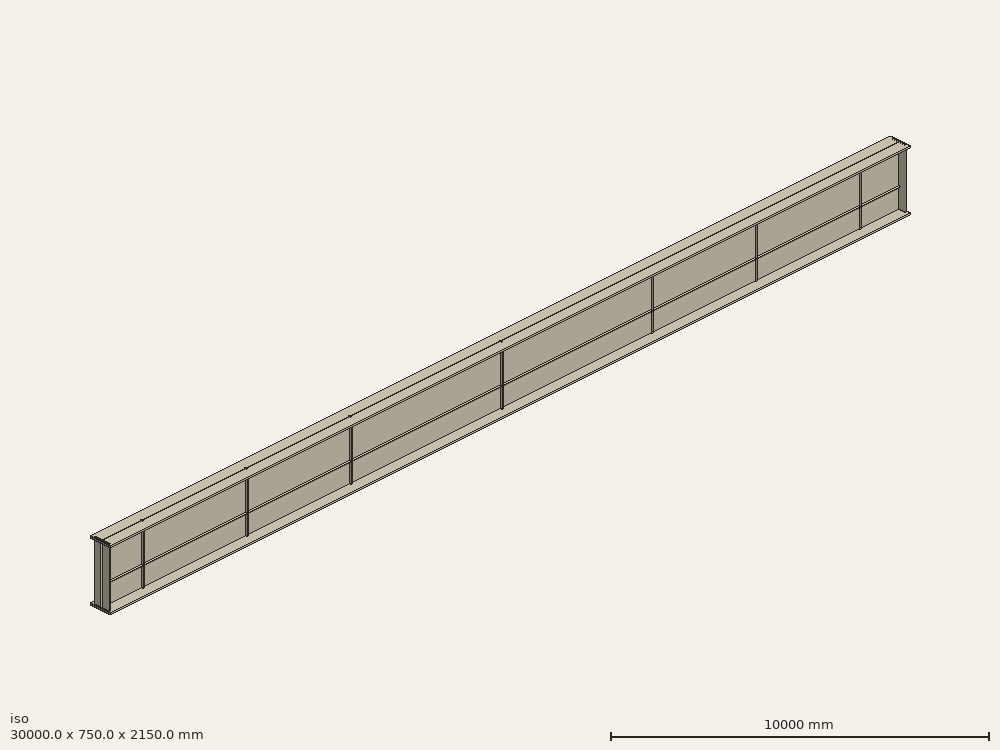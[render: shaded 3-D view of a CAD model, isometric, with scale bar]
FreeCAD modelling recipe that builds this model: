
FCSTD DOCUMENT  (FreeCAD 0.21R33771 (Git))
Label: Plate_girder_EC3_ts
License: All rights reserved
LicenseURL: http://en.wikipedia.org/wiki/All_rights_reserved
objects: Sketcher::SketchObject×13, Part::Extrusion×13, Fem::ConstraintForce×5, Fem::ConstraintDisplacement×2, Fem::FemSolverObjectPython×1, App::MaterialObjectPython×1, Part::Feature×1, Part::FeaturePython×1, Fem::FemMeshObjectPython×1, Fem::FemAnalysis×1
note: 28 computed .brp shape members not serialized (recipe doc carries the construction recipe); baked Part::Feature solids carry a one-line shape summary decoded from their .brp

FEATURE [Fem::FemSolverObjectPython] SolverCcxTools  # FEM object (typed FeaturePython)
  AnalysisType = 4
  BeamShellResultOutput3D = false
  BucklingFactors = 4
  EigenmodeHighLimit = 1000000
  EigenmodeLowLimit = 0
  EigenmodesCount = 10
  GeometricalNonlinearity = 0
  IterationsControlParameterCutb = 0.25,0.5,0.75,0.85,,,1.5,
  IterationsControlParameterIter = 4,8,9,200,10,400,,200,,
  IterationsControlParameterTimeUse = false
  IterationsThermoMechMaximum = 2000
  IterationsUserDefinedIncrementations = false
  IterationsUserDefinedTimeStepLength = false
  MaterialNonlinearity = 0
  MatrixSolverType = 0
  SplitInputWriter = true
  ThermoMechSteadyState = true
  TimeEnd = 1
  TimeInitialStep = 0.01
FEATURE [App::MaterialObjectPython] MaterialSolid  # material (typed FeaturePython)
  Category = 0
  Material = AuthorAndLicense=(c) 2014 M. Münch - GNU Lesser General Public License (LGPL),CardName=Steel-St-E-315,Density=7800 kg/m^3,Father=Metal,+13 more (map truncated)
FEATURE [Sketcher::SketchObject] Sketch001  label="end stiffener"
  FullyConstrained = true
  Placement = pos=(0,0,0) rot=(0.57735,0.57735,0.57735;2.0944rad)
  sketch-geometry (4):
    g0: LineSegment StartX=87.5 StartY=2100 StartZ=0 EndX=662.5 EndY=2100 EndZ=0
    g1: LineSegment StartX=662.5 StartY=2100 StartZ=0 EndX=662.5 EndY=0 EndZ=0
    g2: LineSegment StartX=662.5 StartY=0 StartZ=0 EndX=87.5 EndY=0 EndZ=0
    g3: LineSegment StartX=87.5 StartY=0 StartZ=0 EndX=87.5 EndY=2100 EndZ=0
  constraints (12):
    c: Coincident(g0,g1)
    c: Coincident(g1,g2)
    c: Coincident(g2,g3)
    c: Coincident(g3,g0)
    c: Horizontal(g0)
    c: Horizontal(g2)
    c: Vertical(g1)
    c: Vertical(g3)
    c: DistanceY(g1,g1) = 2100
    c: PointOnObject(g2,g-1)
    c: DistanceX(g2,g2) = 575
    c: DistanceX(g-1,g2) = 87.5
FEATURE [Sketcher::SketchObject] Sketch002  label="stiffener"
  FullyConstrained = true
  Placement = pos=(0,0,0) rot=(0.57735,0.57735,0.57735;2.0944rad)
  sketch-geometry (4):
    g0: LineSegment StartX=287.5 StartY=2100 StartZ=0 EndX=462.5 EndY=2100 EndZ=0
    g1: LineSegment StartX=462.5 StartY=2100 StartZ=0 EndX=462.5 EndY=0 EndZ=0
    g2: LineSegment StartX=462.5 StartY=0 StartZ=0 EndX=287.5 EndY=0 EndZ=0
    g3: LineSegment StartX=287.5 StartY=0 StartZ=0 EndX=287.5 EndY=2100 EndZ=0
  constraints (12):
    c: Coincident(g0,g1)
    c: Coincident(g1,g2)
    c: Coincident(g2,g3)
    c: Coincident(g3,g0)
    c: Horizontal(g0)
    c: Horizontal(g2)
    c: Vertical(g1)
    c: Vertical(g3)
    c: DistanceY(g1,g1) = 2100
    c: PointOnObject(g2,g-1)
    c: DistanceX(g0,g0) = 175
    c: DistanceX(g-1,g2) = 287.5
FEATURE [Sketcher::SketchObject] Sketch003
  FullyConstrained = true
  sketch-geometry (4):
    g0: LineSegment StartX=0 StartY=462.5 StartZ=0 EndX=175 EndY=462.5 EndZ=0
    g1: LineSegment StartX=175 StartY=462.5 StartZ=0 EndX=175 EndY=287.5 EndZ=0
    g2: LineSegment StartX=175 StartY=287.5 StartZ=0 EndX=0 EndY=287.5 EndZ=0
    g3: LineSegment StartX=0 StartY=287.5 StartZ=0 EndX=0 EndY=462.5 EndZ=0
  constraints (12):
    c: Coincident(g0,g1)
    c: Coincident(g1,g2)
    c: Coincident(g2,g3)
    c: Coincident(g3,g0)
    c: Horizontal(g0)
    c: Horizontal(g2)
    c: Vertical(g1)
    c: Vertical(g3)
    c: DistanceX(g0,g0) = 175
    c: DistanceY(g1,g1) = 175
    c: PointOnObject(g2,g-2)
    c: DistanceY(g-1,g2) = 287.5
FEATURE [Part::Extrusion] Extrude001  label="load pad"
  Base = -> Sketch003
  Dir = (0,0,1)
  DirMode = 2
  FaceMakerClass = Part::FaceMakerBullseye
  LengthFwd = 0
  LengthRev = 50
  Placement = pos=(9262.5,0,0) rot=(0,0,1;0rad)
  Solid = true
  Symmetric = false
FEATURE [Part::Extrusion] Extrude002  label="stiffener001"
  Base = -> Sketch002
  Dir = (1,0,0)
  DirMode = 2
  FaceMakerClass = Part::FaceMakerBullseye
  LengthFwd = 15
  LengthRev = 0
  Placement = pos=(1542.5,0,0) rot=(0,0,1;0rad)
  Solid = true
  Symmetric = false
FEATURE [Part::Extrusion] Extrude003  label="end stiffener001"
  Base = -> Sketch001
  Dir = (1,0,0)
  DirMode = 2
  FaceMakerClass = Part::FaceMakerBullseye
  LengthFwd = 24
  LengthRev = 0
  Placement = pos=(50,0,0) rot=(0,0,1;0rad)
  Solid = true
  Symmetric = false
FEATURE [Sketcher::SketchObject] Sketch004  label="end stiffener003"
  FullyConstrained = true
  Placement = pos=(0,0,0) rot=(0.57735,0.57735,0.57735;2.0944rad)
  sketch-geometry (4):
    g0: LineSegment StartX=87.5 StartY=2100 StartZ=0 EndX=662.5 EndY=2100 EndZ=0
    g1: LineSegment StartX=662.5 StartY=2100 StartZ=0 EndX=662.5 EndY=0 EndZ=0
    g2: LineSegment StartX=662.5 StartY=0 StartZ=0 EndX=87.5 EndY=0 EndZ=0
    g3: LineSegment StartX=87.5 StartY=0 StartZ=0 EndX=87.5 EndY=2100 EndZ=0
  constraints (12):
    c: Coincident(g0,g1)
    c: Coincident(g1,g2)
    c: Coincident(g2,g3)
    c: Coincident(g3,g0)
    c: Horizontal(g0)
    c: Horizontal(g2)
    c: Vertical(g1)
    c: Vertical(g3)
    c: DistanceY(g1,g1) = 2100
    c: PointOnObject(g2,g-1)
    c: DistanceX(g2,g2) = 575
    c: DistanceX(g-1,g2) = 87.5
FEATURE [Part::Extrusion] Extrude004  label="end stiffener002"
  Base = -> Sketch004
  Dir = (1,0,0)
  DirMode = 2
  FaceMakerClass = Part::FaceMakerBullseye
  LengthFwd = 24
  LengthRev = 0
  Placement = pos=(29930,0,0) rot=(0,0,1;0rad)
  Solid = true
  Symmetric = false
FEATURE [Sketcher::SketchObject] Sketch005  label="stiffener003"
  FullyConstrained = true
  Placement = pos=(0,0,0) rot=(0.57735,0.57735,0.57735;2.0944rad)
  sketch-geometry (4):
    g0: LineSegment StartX=287.5 StartY=2100 StartZ=0 EndX=462.5 EndY=2100 EndZ=0
    g1: LineSegment StartX=462.5 StartY=2100 StartZ=0 EndX=462.5 EndY=0 EndZ=0
    g2: LineSegment StartX=462.5 StartY=0 StartZ=0 EndX=287.5 EndY=0 EndZ=0
    g3: LineSegment StartX=287.5 StartY=0 StartZ=0 EndX=287.5 EndY=2100 EndZ=0
  constraints (12):
    c: Coincident(g0,g1)
    c: Coincident(g1,g2)
    c: Coincident(g2,g3)
    c: Coincident(g3,g0)
    c: Horizontal(g0)
    c: Horizontal(g2)
    c: Vertical(g1)
    c: Vertical(g3)
    c: DistanceY(g1,g1) = 2100
    c: PointOnObject(g2,g-1)
    c: DistanceX(g0,g0) = 175
    c: DistanceX(g-1,g2) = 287.5
FEATURE [Part::Extrusion] Extrude005  label="stiffener002"
  Base = -> Sketch005
  Dir = (1,0,0)
  DirMode = 2
  FaceMakerClass = Part::FaceMakerBullseye
  LengthFwd = 15
  LengthRev = 0
  Placement = pos=(5442.5,0,0) rot=(0,0,1;0rad)
  Solid = true
  Symmetric = false
FEATURE [Sketcher::SketchObject] Sketch006  label="stiffener005"
  FullyConstrained = true
  Placement = pos=(0,0,0) rot=(0.57735,0.57735,0.57735;2.0944rad)
  sketch-geometry (4):
    g0: LineSegment StartX=287.5 StartY=2100 StartZ=0 EndX=462.5 EndY=2100 EndZ=0
    g1: LineSegment StartX=462.5 StartY=2100 StartZ=0 EndX=462.5 EndY=0 EndZ=0
    g2: LineSegment StartX=462.5 StartY=0 StartZ=0 EndX=287.5 EndY=0 EndZ=0
    g3: LineSegment StartX=287.5 StartY=0 StartZ=0 EndX=287.5 EndY=2100 EndZ=0
  constraints (12):
    c: Coincident(g0,g1)
    c: Coincident(g1,g2)
    c: Coincident(g2,g3)
    c: Coincident(g3,g0)
    c: Horizontal(g0)
    c: Horizontal(g2)
    c: Vertical(g1)
    c: Vertical(g3)
    c: DistanceY(g1,g1) = 2100
    c: PointOnObject(g2,g-1)
    c: DistanceX(g0,g0) = 175
    c: DistanceX(g-1,g2) = 287.5
FEATURE [Part::Extrusion] Extrude006  label="stiffener004"
  Base = -> Sketch006
  Dir = (1,0,0)
  DirMode = 2
  FaceMakerClass = Part::FaceMakerBullseye
  LengthFwd = 15
  LengthRev = 0
  Placement = pos=(9342.5,0,0) rot=(0,0,1;0rad)
  Solid = true
  Symmetric = false
FEATURE [Sketcher::SketchObject] Sketch007  label="stiffener007"
  FullyConstrained = true
  Placement = pos=(0,0,0) rot=(0.57735,0.57735,0.57735;2.0944rad)
  sketch-geometry (4):
    g0: LineSegment StartX=287.5 StartY=2100 StartZ=0 EndX=462.5 EndY=2100 EndZ=0
    g1: LineSegment StartX=462.5 StartY=2100 StartZ=0 EndX=462.5 EndY=0 EndZ=0
    g2: LineSegment StartX=462.5 StartY=0 StartZ=0 EndX=287.5 EndY=0 EndZ=0
    g3: LineSegment StartX=287.5 StartY=0 StartZ=0 EndX=287.5 EndY=2100 EndZ=0
  constraints (12):
    c: Coincident(g0,g1)
    c: Coincident(g1,g2)
    c: Coincident(g2,g3)
    c: Coincident(g3,g0)
    c: Horizontal(g0)
    c: Horizontal(g2)
    c: Vertical(g1)
    c: Vertical(g3)
    c: DistanceY(g1,g1) = 2100
    c: PointOnObject(g2,g-1)
    c: DistanceX(g0,g0) = 175
    c: DistanceX(g-1,g2) = 287.5
FEATURE [Part::Extrusion] Extrude007  label="stiffener006"
  Base = -> Sketch007
  Dir = (1,0,0)
  DirMode = 2
  FaceMakerClass = Part::FaceMakerBullseye
  LengthFwd = 15
  LengthRev = 0
  Placement = pos=(14992.5,0,0) rot=(0,0,1;0rad)
  Solid = true
  Symmetric = false
FEATURE [Sketcher::SketchObject] Sketch008  label="stiffener009"
  FullyConstrained = true
  Placement = pos=(0,0,0) rot=(0.57735,0.57735,0.57735;2.0944rad)
  sketch-geometry (4):
    g0: LineSegment StartX=287.5 StartY=2100 StartZ=0 EndX=462.5 EndY=2100 EndZ=0
    g1: LineSegment StartX=462.5 StartY=2100 StartZ=0 EndX=462.5 EndY=0 EndZ=0
    g2: LineSegment StartX=462.5 StartY=0 StartZ=0 EndX=287.5 EndY=0 EndZ=0
    g3: LineSegment StartX=287.5 StartY=0 StartZ=0 EndX=287.5 EndY=2100 EndZ=0
  constraints (12):
    c: Coincident(g0,g1)
    c: Coincident(g1,g2)
    c: Coincident(g2,g3)
    c: Coincident(g3,g0)
    c: Horizontal(g0)
    c: Horizontal(g2)
    c: Vertical(g1)
    c: Vertical(g3)
    c: DistanceY(g1,g1) = 2100
    c: PointOnObject(g2,g-1)
    c: DistanceX(g0,g0) = 175
    c: DistanceX(g-1,g2) = 287.5
FEATURE [Part::Extrusion] Extrude008  label="stiffener008"
  Base = -> Sketch008
  Dir = (1,0,0)
  DirMode = 2
  FaceMakerClass = Part::FaceMakerBullseye
  LengthFwd = 15
  LengthRev = 0
  Placement = pos=(20642.5,0,0) rot=(0,0,1;0rad)
  Solid = true
  Symmetric = false
FEATURE [Sketcher::SketchObject] Sketch009  label="stiffener011"
  FullyConstrained = true
  Placement = pos=(0,0,0) rot=(0.57735,0.57735,0.57735;2.0944rad)
  sketch-geometry (4):
    g0: LineSegment StartX=287.5 StartY=2100 StartZ=0 EndX=462.5 EndY=2100 EndZ=0
    g1: LineSegment StartX=462.5 StartY=2100 StartZ=0 EndX=462.5 EndY=0 EndZ=0
    g2: LineSegment StartX=462.5 StartY=0 StartZ=0 EndX=287.5 EndY=0 EndZ=0
    g3: LineSegment StartX=287.5 StartY=0 StartZ=0 EndX=287.5 EndY=2100 EndZ=0
  constraints (12):
    c: Coincident(g0,g1)
    c: Coincident(g1,g2)
    c: Coincident(g2,g3)
    c: Coincident(g3,g0)
    c: Horizontal(g0)
    c: Horizontal(g2)
    c: Vertical(g1)
    c: Vertical(g3)
    c: DistanceY(g1,g1) = 2100
    c: PointOnObject(g2,g-1)
    c: DistanceX(g0,g0) = 175
    c: DistanceX(g-1,g2) = 287.5
FEATURE [Part::Extrusion] Extrude009  label="stiffener010"
  Base = -> Sketch009
  Dir = (1,0,0)
  DirMode = 2
  FaceMakerClass = Part::FaceMakerBullseye
  LengthFwd = 15
  LengthRev = 0
  Placement = pos=(24542.5,0,0) rot=(0,0,1;0rad)
  Solid = true
  Symmetric = false
FEATURE [Sketcher::SketchObject] Sketch010  label="stiffener013"
  FullyConstrained = true
  Placement = pos=(0,0,0) rot=(0.57735,0.57735,0.57735;2.0944rad)
  sketch-geometry (4):
    g0: LineSegment StartX=287.5 StartY=2100 StartZ=0 EndX=462.5 EndY=2100 EndZ=0
    g1: LineSegment StartX=462.5 StartY=2100 StartZ=0 EndX=462.5 EndY=0 EndZ=0
    g2: LineSegment StartX=462.5 StartY=0 StartZ=0 EndX=287.5 EndY=0 EndZ=0
    g3: LineSegment StartX=287.5 StartY=0 StartZ=0 EndX=287.5 EndY=2100 EndZ=0
  constraints (12):
    c: Coincident(g0,g1)
    c: Coincident(g1,g2)
    c: Coincident(g2,g3)
    c: Coincident(g3,g0)
    c: Horizontal(g0)
    c: Horizontal(g2)
    c: Vertical(g1)
    c: Vertical(g3)
    c: DistanceY(g1,g1) = 2100
    c: PointOnObject(g2,g-1)
    c: DistanceX(g0,g0) = 175
    c: DistanceX(g-1,g2) = 287.5
FEATURE [Part::Extrusion] Extrude010  label="stiffener012"
  Base = -> Sketch010
  Dir = (1,0,0)
  DirMode = 2
  FaceMakerClass = Part::FaceMakerBullseye
  LengthFwd = 15
  LengthRev = 0
  Placement = pos=(28442.5,0,0) rot=(0,0,1;0rad)
  Solid = true
  Symmetric = false
FEATURE [Sketcher::SketchObject] Sketch  label="girder"
  FullyConstrained = true
  Placement = pos=(0,0,0) rot=(0.57735,0.57735,0.57735;2.0944rad)
  sketch-geometry (16):
    g0: LineSegment StartX=750 StartY=2100 StartZ=0 EndX=750 EndY=2050 EndZ=0
    g1: LineSegment StartX=750 StartY=2050 StartZ=0 EndX=382.5 EndY=2050 EndZ=0
    g2: LineSegment StartX=382.5 StartY=2050 StartZ=0 EndX=382.5 EndY=50 EndZ=0
    g3: LineSegment StartX=382.5 StartY=50 StartZ=0 EndX=750 EndY=50 EndZ=0
    g4: LineSegment StartX=750 StartY=50 StartZ=0 EndX=750 EndY=0 EndZ=0
    g5: LineSegment StartX=0 StartY=0 StartZ=0 EndX=0 EndY=50 EndZ=0
    g6: LineSegment StartX=0 StartY=50 StartZ=0 EndX=367.5 EndY=50 EndZ=0
    g7: LineSegment StartX=367.5 StartY=50 StartZ=0 EndX=367.5 EndY=2050 EndZ=0
    g8: LineSegment StartX=367.5 StartY=2050 StartZ=0 EndX=0 EndY=2050 EndZ=0
    g9: LineSegment StartX=750 StartY=2100 StartZ=0 EndX=382.5 EndY=2100 EndZ=0
    g10: LineSegment StartX=750 StartY=0 StartZ=0 EndX=382.5 EndY=0 EndZ=0
    g11: LineSegment StartX=367.5 StartY=0 StartZ=0 EndX=0 EndY=0 EndZ=0
    g12: LineSegment StartX=382.5 StartY=2100 StartZ=0 EndX=367.5 EndY=2100 EndZ=0
    g13: LineSegment StartX=0 StartY=2050 StartZ=0 EndX=0 EndY=2100 EndZ=0
    g14: LineSegment StartX=367.5 StartY=0 StartZ=0 EndX=382.5 EndY=0 EndZ=0
    g15: LineSegment StartX=0 StartY=2100 StartZ=0 EndX=367.5 EndY=2100 EndZ=0
  constraints (48):
    c: Vertical(g0)
    c: Coincident(g0,g1)
    c: Horizontal(g1)
    c: Coincident(g1,g2)
    c: Vertical(g2)
    c: Coincident(g2,g3)
    c: Horizontal(g3)
    c: Coincident(g3,g4)
    c: PointOnObject(g4,g-1)
    c: Vertical(g5)
    c: Coincident(g5,g6)
    c: Horizontal(g6)
    c: Coincident(g6,g7)
    c: Vertical(g7)
    c: Coincident(g7,g8)
    c: Horizontal(g8)
    c: Vertical(g4)
    c: DistanceY(g0,g0) = 50
    c: DistanceX(g6,g6) = 367.5
    c: DistanceX(g3,g3) = 367.5
    c: DistanceY(g4,g4) = 50
    c: DistanceY(g5,g5) = 50
    c: DistanceY(g4,g0) = 2100
    c: DistanceX(g-1,g5) = 0
    c: Coincident(g9,g0)
    c: Horizontal(g9)
    c: Coincident(g10,g4)
    c: Horizontal(g10)
    c: Coincident(g11,g5)
    c: Horizontal(g11)
    c: Coincident(g12,g9)
    c: Horizontal(g12)
    c: Coincident(g13,g8)
    c: Vertical(g13)
    c: DistanceX(g7,g1) = 15
    c: Equal(g11,g6)
    c: Equal(g10,g3)
    c: Coincident(g14,g11)
    c: Coincident(g14,g10)
    c: DistanceY(g13,g13) = 50
    c: DistanceY(g-1,g5) = 0
    c: Coincident(g15,g13)
    c: Coincident(g15,g12)
    c: Horizontal(g15)
    c: DistanceX(g15,g15) = 367.5
    c: DistanceX(g12,g12) = 15
    c: DistanceX(g9,g9) = 367.5
    c: PointOnObject(g13,g-2)
FEATURE [Part::Extrusion] Extrude
  Base = -> Sketch
  Dir = (1,0,0)
  DirMode = 2
  FaceMakerClass = Part::FaceMakerBullseye
  LengthFwd = 30000
  LengthRev = 0
  Solid = true
  Symmetric = false
FEATURE [Sketcher::SketchObject] Sketch011
  FullyConstrained = true
  sketch-geometry (4):
    g0: LineSegment StartX=0 StartY=462.5 StartZ=0 EndX=175 EndY=462.5 EndZ=0
    g1: LineSegment StartX=175 StartY=462.5 StartZ=0 EndX=175 EndY=287.5 EndZ=0
    g2: LineSegment StartX=175 StartY=287.5 StartZ=0 EndX=0 EndY=287.5 EndZ=0
    g3: LineSegment StartX=0 StartY=287.5 StartZ=0 EndX=0 EndY=462.5 EndZ=0
  constraints (12):
    c: Coincident(g0,g1)
    c: Coincident(g1,g2)
    c: Coincident(g2,g3)
    c: Coincident(g3,g0)
    c: Horizontal(g0)
    c: Horizontal(g2)
    c: Vertical(g1)
    c: Vertical(g3)
    c: DistanceX(g0,g0) = 175
    c: DistanceY(g1,g1) = 175
    c: PointOnObject(g2,g-2)
    c: DistanceY(g-1,g2) = 287.5
FEATURE [Part::Extrusion] Extrude011  label="load pad001"
  Base = -> Sketch011
  Dir = (0,0,1)
  DirMode = 2
  FaceMakerClass = Part::FaceMakerBullseye
  LengthFwd = 0
  LengthRev = 50
  Placement = pos=(20562.5,0,0) rot=(0,0,1;0rad)
  Solid = true
  Symmetric = false
FEATURE [Part::Feature] Extrude013  label="stiffener_horizontal"
  Placement = pos=(0,0,750) rot=(0,0,1;0rad)
  shape: bbox 29860 x 175 x 15 mm, 6 faces (baked)
FEATURE [Part::FeaturePython] BooleanFragments  # WARN: FeaturePython — macro-defined, semantics opaque (R4)
  Mode = 2
  Objects = -> [Extrude001,Extrude002,Extrude003,Extrude004,Extrude005,Extrude006,Extrude007,Extrude008,Extrude009,Extrude010,Extrude,Extrude011,Extrude013]
  Tolerance = 0
FEATURE [Fem::FemMeshObjectPython] FEMMeshGmsh  # FEM object (typed FeaturePython)
  Algorithm2D = 0
  Algorithm3D = 0
  CharacteristicLengthMax = 290
  CharacteristicLengthMin = 0
  CoherenceMesh = true
  ElementDimension = 0
  ElementOrder = 1
  GeometryTolerance = 1e-06
  GroupsOfNodes = false
  HighOrderOptimize = 0
  MeshSizeFromCurvature = 12
  OptimizeNetgen = false
  OptimizeStd = true
  Part = -> BooleanFragments
  RecombinationAlgorithm = 0
  Recombine3DAll = false
  RecombineAll = false
  SecondOrderLinear = false
FEATURE [Fem::ConstraintDisplacement] ConstraintDisplacement003
  NormalDirection = (0,0,1)
  Normals = (10) [(0,0,1),(0,0,1),(0,0,1),(0,0,1),(0,0,1),(0,0,1),(0,0,1),(0,0,1),(0,0,1),(0,0,1)]
  Points = (10) [(50,382.5,2100),(50,475.833,2100),(50,569.167,2100),(50,662.5,2100),(50,367.5,2100),(50,382.5,2100),(50,87.5,2100),(50,180.833,2100),+2 more]
  References = -> [BooleanFragments]
  Scale = 18
  hasXFormula = false
  hasYFormula = false
  hasZFormula = false
  rotxFix = false
  rotxFree = true
  rotyFix = false
  rotyFree = true
  rotzFix = false
  rotzFree = true
  useFlowSurfaceForce = false
  xDisplacement = 0
  xFix = false
  xFree = false
  xRotation = 0
  yDisplacement = 0
  yFix = false
  yFree = false
  yRotation = 0
  zDisplacement = 0
  zFix = false
  zFree = false
  zRotation = 0
FEATURE [Fem::ConstraintDisplacement] ConstraintDisplacement004
  NormalDirection = (0,0,1)
  Normals = (10) [(0,0,1),(0,0,1),(0,0,1),(0,0,1),(0,0,1),(0,0,1),(0,0,1),(0,0,1),(0,0,1),(0,0,1)]
  Points = (10) [(29954,382.5,2100),(29954,475.833,2100),(29954,569.167,2100),(29954,662.5,2100),(29954,367.5,2100),(29954,382.5,2100),(29954,87.5,2100),+3 more]
  References = -> [BooleanFragments]
  Scale = 18
  hasXFormula = false
  hasYFormula = false
  hasZFormula = false
  rotxFix = false
  rotxFree = true
  rotyFix = false
  rotyFree = true
  rotzFix = false
  rotzFree = true
  useFlowSurfaceForce = false
  xDisplacement = 0
  xFix = false
  xFree = true
  xRotation = 0
  yDisplacement = 0
  yFix = false
  yFree = false
  yRotation = 0
  zDisplacement = 0
  zFix = false
  zFree = false
  zRotation = 0
FEATURE [Fem::ConstraintForce] ConstraintForce005
  DirectionVector = (0,0,-1)
  Force = 2293000
  NormalDirection = (0,0,1)
  Points = (33) [(74,382.5,2100),(74,475.833,2100),(74,569.167,2100),(74,662.5,2100),(62,382.5,2100),(62,475.833,2100),(62,569.167,2100),(62,662.5,2100),+25 more]
  References = -> [BooleanFragments]
  Reversed = true
  Scale = 13
FEATURE [Fem::ConstraintForce] ConstraintForce006
  DirectionVector = (0,0,-1)
  Force = 2293000
  NormalDirection = (0,0,1)
  Points = (33) [(29954,382.5,2100),(29954,475.833,2100),(29954,569.167,2100),(29954,662.5,2100),(29942,382.5,2100),(29942,475.833,2100),(29942,569.167,2100),+26 more]
  References = -> [BooleanFragments]
  Reversed = true
  Scale = 13
FEATURE [Fem::ConstraintForce] ConstraintForce007
  DirectionVector = (0,0,1)
  Force = 925000
  NormalDirection = (0,0,-1)
  Points = (16) [(9262.5,287.5,-50),(9320.83,287.5,-50),(9379.17,287.5,-50),(9437.5,287.5,-50),(9262.5,345.833,-50),(9320.83,345.833,-50),(9379.17,345.833,-50),+9 more]
  References = -> [BooleanFragments]
  Reversed = true
  Scale = 14
FEATURE [Fem::ConstraintForce] ConstraintForce008
  DirectionVector = (0,0,1)
  Force = 925000
  NormalDirection = (0,0,-1)
  Points = (16) [(20562.5,287.5,-50),(20620.8,287.5,-50),(20679.2,287.5,-50),(20737.5,287.5,-50),(20562.5,345.833,-50),(20620.8,345.833,-50),(20679.2,345.833,-50),+9 more]
  References = -> [BooleanFragments]
  Reversed = true
  Scale = 14
FEATURE [Fem::ConstraintForce] ConstraintForce009
  DirectionVector = (0,0,1)
  Force = 2736000
  NormalDirection = (0,0,-1)
  Points = (315) [(50,367.5,0),(50,375,0),(50,382.5,0),(33.3333,367.5,0),(33.3333,375,0),(33.3333,382.5,0),(16.6667,367.5,0),(16.6667,375,0),(16.6667,382.5,0),+306 more]
  References = -> [BooleanFragments]
  Reversed = true
FEATURE [Fem::FemAnalysis] Analysis
  Group = -> [SolverCcxTools,MaterialSolid,FEMMeshGmsh,ConstraintDisplacement003,ConstraintDisplacement004,ConstraintForce005,ConstraintForce006,ConstraintForce007,ConstraintForce008,ConstraintForce009]
FEATURE [Sketcher::SketchObject] Sketch012
  ExternalGeometry = -> [BooleanFragments]
  FullyConstrained = true
  sketch-geometry (4):
    g0: LineSegment StartX=1557.5 StartY=382.5 StartZ=0 EndX=74 EndY=382.5 EndZ=0
    g1: LineSegment StartX=74 StartY=382.5 StartZ=0 EndX=74 EndY=382.5 EndZ=0
    g2: LineSegment StartX=74 StartY=382.5 StartZ=0 EndX=1557.5 EndY=382.5 EndZ=0
    g3: LineSegment StartX=1557.5 StartY=382.5 StartZ=0 EndX=1557.5 EndY=382.5 EndZ=0
  constraints (12):
    c: Coincident(g0,g1)
    c: Coincident(g1,g2)
    c: Coincident(g2,g3)
    c: Coincident(g3,g0)
    c: Horizontal(g0)
    c: Horizontal(g2)
    c: Vertical(g1)
    c: Vertical(g3)
    c: Vertical(g0,g-4)
    c: Vertical(g3,g-3)
    c: PointOnObject(g-5,g0)
    c: PointOnObject(g-6,g2)
FEATURE [Part::Extrusion] Extrude012
  Base = -> Sketch012
  Dir = (0,0,1)
  DirMode = 2
  FaceMakerClass = Part::FaceMakerBullseye
  LengthFwd = 15
  LengthRev = 0
  Placement = pos=(0,0,600) rot=(0,0,1;0rad)
  Solid = true
  Symmetric = false
